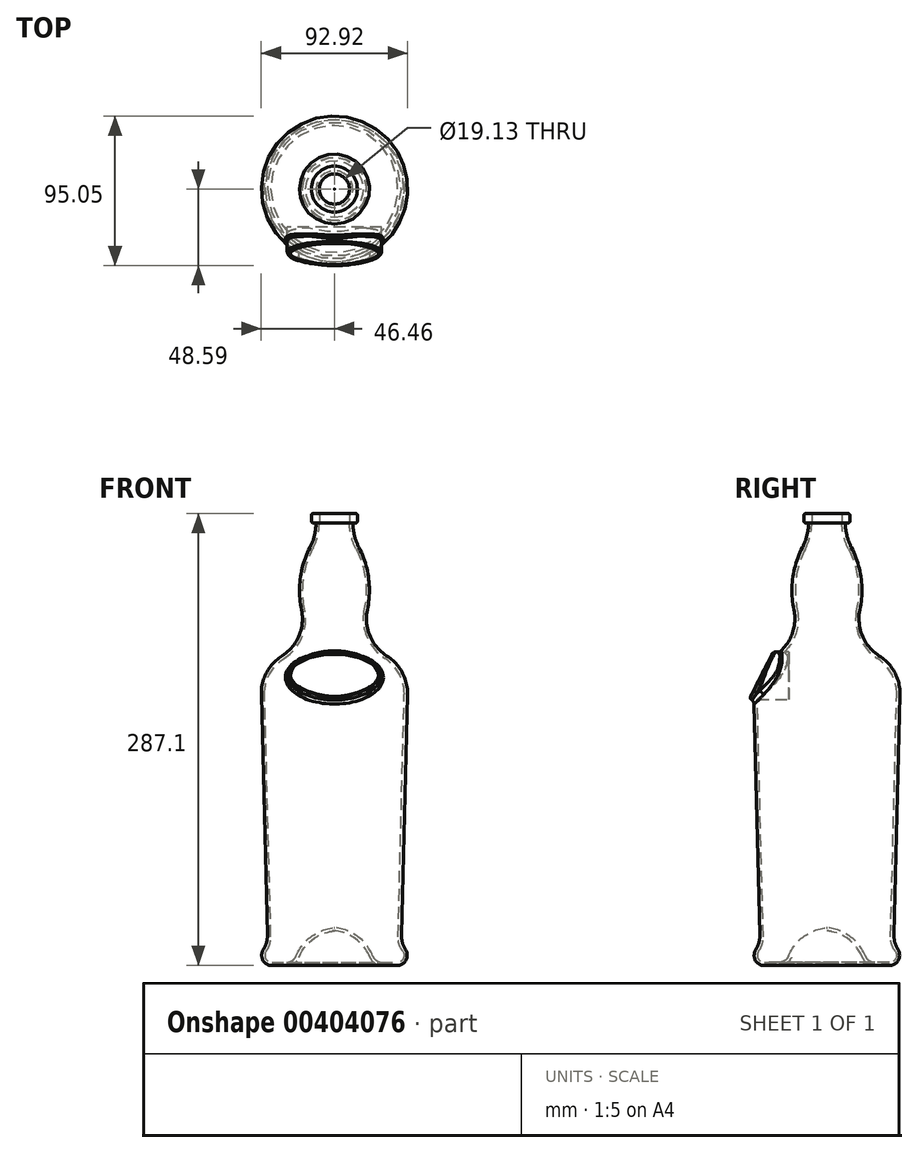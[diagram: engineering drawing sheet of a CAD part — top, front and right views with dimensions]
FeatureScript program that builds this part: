
annotation { "Feature Type Name" : "Feature", "Feature Type Description" : "" }
export const myFeature = defineFeature(function(context is Context, id is Id, definition is map)
    precondition{}
    {
        {
            var Q0;
            Q0=qCreatedBy(makeId("Front.planeOp"),FACE);
            var sketch = newSketch(context, id + "F0", { "sketchPlane" : qUnion([Q0])});
            skLineSegment(sketch, "E0", {"start": v(30.45, 0.13) * mm, "end": v(39.69, 0.13) * mm});
            skArc(sketch, "E1", {"start": v(39.69, 0.13) * mm, "mid": v(45.41, 3.52) * mm, "end": v(45.2, 10.17) * mm});
            skLineSegment(sketch, "E2.trimOffspring", {"start": v(42.6, 19.54) * mm, "end": v(46.45, 171.94) * mm});
            skArc(sketch, "E3", {"start": v(20.93, 226.15) * mm, "mid": v(22.49, 209.63) * mm, "end": v(33.17, 196.93) * mm});
            skArc(sketch, "E4", {"start": v(22.49, 5.48) * mm, "mid": v(13.58, 16.96) * mm, "end": v(0, 22.15) * mm});
            skArc(sketch, "E5", {"start": v(22.49, 5.48) * mm, "mid": v(25.65, 1.6) * mm, "end": v(30.45, 0.13) * mm});
            skArc(sketch, "E6", {"start": v(46.45, 171.94) * mm, "mid": v(43.1, 186.18) * mm, "end": v(33.17, 196.93) * mm});
            skLineSegment(sketch, "E7.bottom", {"start": v(10.27, 287.23) * mm, "end": v(13.58, 287.23) * mm});
            skLineSegment(sketch, "E7.top", {"start": v(13.08, 281.12) * mm, "end": v(13.18, 281.12) * mm});
            skLineSegment(sketch, "E7.left", {"start": v(9.57, 286.52) * mm, "end": v(9.57, 281.12) * mm});
            skLineSegment(sketch, "E7.right", {"start": v(14.58, 286.22) * mm, "end": v(14.58, 282.53) * mm});
            skArc(sketch, "E8", {"start": v(11.73, 279.7) * mm, "mid": v(12.94, 272.43) * mm, "end": v(15.62, 265.57) * mm});
            skArc(sketch, "E9", {"start": v(20.93, 226.15) * mm, "mid": v(21.7, 246.32) * mm, "end": v(15.62, 265.57) * mm});
            skPoint(sketch, "E10.visualSharp", {"position": v(11.67, 281.12) * mm});
            skArc(sketch, "E10.filletArc", {"start": v(13.08, 281.12) * mm, "mid": v(12.1, 280.7) * mm, "end": v(11.73, 279.7) * mm});
            skPoint(sketch, "E11.visualSharp", {"position": v(14.58, 281.12) * mm});
            skArc(sketch, "E11.filletArc", {"start": v(13.18, 281.12) * mm, "mid": v(14.17, 281.53) * mm, "end": v(14.58, 282.53) * mm});
            skPoint(sketch, "E12.visualSharp", {"position": v(14.58, 287.23) * mm});
            skArc(sketch, "E12.filletArc", {"start": v(14.58, 286.22) * mm, "mid": v(14.3, 286.93) * mm, "end": v(13.58, 287.23) * mm});
            skPoint(sketch, "E13.visualSharp", {"position": v(9.57, 287.23) * mm});
            skArc(sketch, "E13.filletArc", {"start": v(10.27, 287.23) * mm, "mid": v(9.77, 287.02) * mm, "end": v(9.57, 286.52) * mm});
            skArc(sketch, "E14.1", {"start": v(9.6, 280.4) * mm, "mid": v(10.8, 272.28) * mm, "end": v(13.76, 264.6) * mm});
            skArc(sketch, "E14.2", {"start": v(18.88, 226.59) * mm, "mid": v(19.6, 246.04) * mm, "end": v(13.76, 264.6) * mm});
            skArc(sketch, "E14.3", {"start": v(18.88, 226.59) * mm, "mid": v(20.55, 208.82) * mm, "end": v(32.04, 195.16) * mm});
            skArc(sketch, "E14.4", {"start": v(44.35, 171.9) * mm, "mid": v(41.26, 185.15) * mm, "end": v(32.04, 195.16) * mm});
            skLineSegment(sketch, "E15", {"start": v(9.57, 281.12) * mm, "end": v(9.6, 280.4) * mm});
            skArc(sketch, "E16.1", {"start": v(24.34, 6.24) * mm, "mid": v(14.77, 18.57) * mm, "end": v(0.18, 24.14) * mm});
            skArc(sketch, "E16.2", {"start": v(24.34, 6.24) * mm, "mid": v(26.77, 3.25) * mm, "end": v(30.45, 2.13) * mm});
            skLineSegment(sketch, "E16.3", {"start": v(30.45, 2.13) * mm, "end": v(39.69, 2.13) * mm});
            skArc(sketch, "E16.4", {"start": v(39.69, 2.13) * mm, "mid": v(43.74, 4.64) * mm, "end": v(43.3, 9.39) * mm});
            skLineSegment(sketch, "E17", {"start": v(0, 22.15) * mm, "end": v(0, 24.14) * mm});
            skLineSegment(sketch, "E18", {"start": v(0, 24.14) * mm, "end": v(0.18, 24.14) * mm});
            skArc(sketch, "E19", {"start": v(42.6, 19.54) * mm, "mid": v(43.2, 14.66) * mm, "end": v(45.2, 10.17) * mm});
            skArc(sketch, "E20", {"start": v(40.42, 18.35) * mm, "mid": v(41.1, 13.63) * mm, "end": v(43.3, 9.39) * mm});
            skLineSegment(sketch, "E21", {"start": v(40.42, 18.35) * mm, "end": v(44.35, 171.9) * mm});
            skSolve(sketch);
        }
        {
            var Q0;
            Q0=makeQuery(id+"F0.imprint","IMPRINT",FACE,{"disambiguationData":[TD([[makeQuery(id+"F0.imprint","IMPRINT",EDGE,{"derivedFrom":sQuery(id+"F0.wireOp",EDGE,"E0")}),1.0]])]});
            var Q1;
            Q1=sQuery(id+"F0.wireOp",EDGE,"E17");
            revolve(context, id + "F1", {"entities" : qUnion([Q0]), "axis" : qUnion([Q1]), "revolveType" : RevolveType.FULL});
        }
        {
            var Q0;
            Q0=qCreatedBy(makeId("Front.planeOp"),FACE);
            var sketch = newSketch(context, id + "F2", { "sketchPlane" : qUnion([Q0])});
            skEllipse(sketch, "E22", {"center": v(0, 184.17) * mm, "majorRadius": 30 * mm, "minorRadius": 15 * mm, "majorAxis": v(1, 0)});
            skSolve(sketch);
        }
        {
            var Q0;
            Q0 = qSketchRegion(id + "F2", true);
            extrude(context, id + "F3", {"entities" : qUnion([Q0]), "operationType" : NewBodyOperationType.ADD, "depth" : 65.8 * mm, "hasSecondDirection" : true, "secondDirectionOppositeDirection" : false, "secondDirectionDepth" : 24 * mm});
        }
        {
            var Q0;
            Q0=qCreatedBy(makeId("Right.planeOp"),FACE);
            var sketch = newSketch(context, id + "F4", { "sketchPlane" : qUnion([Q0])});
            skLineSegment(sketch, "E23", {"start": v(-30, 207.5) * mm, "end": v(-52.35, 163.44) * mm});
            skLineSegment(sketch, "E24", {"start": v(-52.35, 163.44) * mm, "end": v(-86.95, 163.44) * mm});
            skLineSegment(sketch, "E25", {"start": v(-86.95, 163.44) * mm, "end": v(-86.95, 207.5) * mm});
            skLineSegment(sketch, "E26", {"start": v(-86.95, 207.5) * mm, "end": v(-30, 207.5) * mm});
            skSolve(sketch);
        }
        {
            var Q0;
            Q0=makeQuery(id+"F4.imprint","IMPRINT",FACE,{"disambiguationData":[TD([[makeQuery(id+"F4.imprint","IMPRINT",EDGE,{"derivedFrom":sQuery(id+"F4.wireOp",EDGE,"E23")}),-1.0]])]});
            extrude(context, id + "F5", {"entities" : qUnion([Q0]), "endBound" : BoundingType.SYMMETRIC, "depth" : 68.8 * mm});
        }
        {
            var Q0;
            Q0=makeQuery(id+"F5.opExtrude","SWEPT_BODY",BODY,{"disambiguationData":[OSD([sQuery(id+"F4.wireOp",EDGE,"E23"),sQuery(id+"F4.wireOp",EDGE,"E24"),sQuery(id+"F4.wireOp",EDGE,"E25"),sQuery(id+"F4.wireOp",EDGE,"E26")])]});
            var Q1;
            Q1=makeQuery(id+"F1.opRevolve","SWEPT_BODY",BODY,{"disambiguationData":[OSD([sQuery(id+"F0.wireOp",EDGE,"E0"),sQuery(id+"F0.wireOp",EDGE,"E1"),sQuery(id+"F0.wireOp",EDGE,"E2.trimOffspring"),sQuery(id+"F0.wireOp",EDGE,"E3"),sQuery(id+"F0.wireOp",EDGE,"E4"),sQuery(id+"F0.wireOp",EDGE,"E5"),sQuery(id+"F0.wireOp",EDGE,"E6"),sQuery(id+"F0.wireOp",EDGE,"E7.bottom"),sQuery(id+"F0.wireOp",EDGE,"E7.top"),sQuery(id+"F0.wireOp",EDGE,"E7.left"),sQuery(id+"F0.wireOp",EDGE,"E7.right"),sQuery(id+"F0.wireOp",EDGE,"E8"),sQuery(id+"F0.wireOp",EDGE,"E9"),sQuery(id+"F0.wireOp",EDGE,"E10.filletArc"),sQuery(id+"F0.wireOp",EDGE,"E11.filletArc"),sQuery(id+"F0.wireOp",EDGE,"E12.filletArc"),sQuery(id+"F0.wireOp",EDGE,"E13.filletArc"),sQuery(id+"F0.wireOp",EDGE,"E14.1"),sQuery(id+"F0.wireOp",EDGE,"E14.2"),sQuery(id+"F0.wireOp",EDGE,"E14.3"),sQuery(id+"F0.wireOp",EDGE,"E14.4"),sQuery(id+"F0.wireOp",EDGE,"E15"),sQuery(id+"F0.wireOp",EDGE,"E16.1"),sQuery(id+"F0.wireOp",EDGE,"E16.2"),sQuery(id+"F0.wireOp",EDGE,"E16.3"),sQuery(id+"F0.wireOp",EDGE,"E16.4"),sQuery(id+"F0.wireOp",EDGE,"E17"),sQuery(id+"F0.wireOp",EDGE,"E18"),sQuery(id+"F0.wireOp",EDGE,"E19"),sQuery(id+"F0.wireOp",EDGE,"E20"),sQuery(id+"F0.wireOp",EDGE,"E21")])]});
            booleanBodies(context, id + "F6", {"operationType" : BooleanOperationType.SUBTRACTION, "tools" : qUnion([Q0]), "targets" : qUnion([Q1])});
        }
        {
            var Q0;
            Q0=makeQuery(id+"F3.boolean.opBoolean","INTERSECT",EDGE,{"derivedFrom":[makeQuery(id+"F1.opRevolve","SWEPT_FACE",FACE,{"disambiguationData":[OSD([sQuery(id+"F0.wireOp",EDGE,"E3")])]}),makeQuery(id+"F3.opExtrude","SWEPT_FACE",FACE,{"disambiguationData":[OSD([sQuery(id+"F2.wireOp",EDGE,"E22")])]})]});
            var Q1;
            Q1=makeQuery(id+"F3.boolean.opBoolean","INTERSECT",EDGE,{"disambiguationData":[OD(0.0)],"derivedFrom":[makeQuery(id+"F1.opRevolve","SWEPT_FACE",FACE,{"disambiguationData":[OSD([sQuery(id+"F0.wireOp",EDGE,"E6")])]}),makeQuery(id+"F3.opExtrude","SWEPT_FACE",FACE,{"disambiguationData":[OSD([sQuery(id+"F2.wireOp",EDGE,"E22")])]})]});
            var Q2;
            Q2=makeQuery(id+"F3.boolean.opBoolean","INTERSECT",EDGE,{"derivedFrom":[makeQuery(id+"F1.opRevolve","SWEPT_FACE",FACE,{"disambiguationData":[OSD([sQuery(id+"F0.wireOp",EDGE,"E2.trimOffspring")])]}),makeQuery(id+"F3.opExtrude","SWEPT_FACE",FACE,{"disambiguationData":[OSD([sQuery(id+"F2.wireOp",EDGE,"E22")])]})]});
            var Q3;
            Q3=makeQuery(id+"F3.boolean.opBoolean","INTERSECT",EDGE,{"disambiguationData":[OD(1.0)],"derivedFrom":[makeQuery(id+"F1.opRevolve","SWEPT_FACE",FACE,{"disambiguationData":[OSD([sQuery(id+"F0.wireOp",EDGE,"E6")])]}),makeQuery(id+"F3.opExtrude","SWEPT_FACE",FACE,{"disambiguationData":[OSD([sQuery(id+"F2.wireOp",EDGE,"E22")])]})]});
            fillet(context, id + "F7", {"entities" : qUnion([Q0, Q1, Q2, Q3]), "radius" : 3 * mm, "tangentPropagation" : true, "allowEdgeOverflow" : false});
        }
        {
            var Q0;
            {var subQ0=sQuery(id+"F2.wireOp",EDGE,"E22");Q0=makeQuery(id+"F6.opBoolean","INTERSECT",EDGE,{"derivedFrom":[makeQuery(id+"F3.boolean.opBoolean","SPLIT",FACE,{"disambiguationData":[TD([makeQuery(id+"F1.opRevolve","SWEPT_FACE",FACE,{"disambiguationData":[OSD([sQuery(id+"F0.wireOp",EDGE,"E2.trimOffspring")])]})])],"derivedFrom":makeQuery(id+"F3.opExtrude","SWEPT_FACE",FACE,{"disambiguationData":[OSD([subQ0])]})}),makeQuery(id+"F5.opExtrude","SWEPT_FACE",FACE,{"disambiguationData":[OSD([sQuery(id+"F4.wireOp",EDGE,"E23")])]})]});}
            fillet(context, id + "F8", {"entities" : qUnion([Q0]), "radius" : 2 * mm, "tangentPropagation" : true, "allowEdgeOverflow" : false});
        }
        {
            var Q0;
            Q0=makeQuery(id+"F6.opBoolean","COPY",FACE,{"derivedFrom":makeQuery(id+"F5.opExtrude","SWEPT_FACE",FACE,{"disambiguationData":[OSD([sQuery(id+"F4.wireOp",EDGE,"E23")])]})});
            extrude(context, id + "F9", {"entities" : qUnion([Q0]), "operationType" : NewBodyOperationType.REMOVE, "oppositeDirection" : true, "depth" : 1.5 * mm});
        }
        {
            var Q0;
            {var subQ0=sQuery(id+"F4.wireOp",EDGE,"E23");var subQ1=makeQuery(id+"F5.opExtrude","SWEPT_FACE",FACE,{"disambiguationData":[OSD([subQ0])]});var subQ2=sQuery(id+"F2.wireOp",EDGE,"E22");var subQ3=makeQuery(id+"F8.opFillet","BLEND_EDGE",EDGE,{"disambiguationData":[OD(1.0)],"blendedFrom":[makeQuery(id+"F6.opBoolean","INTERSECT",EDGE,{"derivedFrom":[makeQuery(id+"F3.boolean.opBoolean","SPLIT",FACE,{"disambiguationData":[TD([makeQuery(id+"F1.opRevolve","SWEPT_FACE",FACE,{"disambiguationData":[OSD([sQuery(id+"F0.wireOp",EDGE,"E2.trimOffspring")])]})])],"derivedFrom":makeQuery(id+"F3.opExtrude","SWEPT_FACE",FACE,{"disambiguationData":[OSD([subQ2])]})}),subQ1]}),makeQuery(id+"F6.opBoolean","COPY",FACE,{"derivedFrom":subQ1})],"blendedInto":[makeQuery(id+"F6.opBoolean","COPY",FACE,{"derivedFrom":subQ1})]});Q0=makeQuery(id+"F9.boolean.opBoolean","MERGE",EDGE,{"derivedFrom":[subQ3,makeQuery(id+"F9.opExtrude","CAP_EDGE",EDGE,{"disambiguationData":[OSD([subQ2,subQ0]),TDD([subQ3])],"isStart":true})]});}
            var Q1;
            {var subQ0=sQuery(id+"F4.wireOp",EDGE,"E23");var subQ1=makeQuery(id+"F5.opExtrude","SWEPT_FACE",FACE,{"disambiguationData":[OSD([subQ0])]});var subQ2=sQuery(id+"F2.wireOp",EDGE,"E22");var subQ3=makeQuery(id+"F8.opFillet","BLEND_EDGE",EDGE,{"disambiguationData":[OD(0.0)],"blendedFrom":[makeQuery(id+"F6.opBoolean","INTERSECT",EDGE,{"derivedFrom":[makeQuery(id+"F3.boolean.opBoolean","SPLIT",FACE,{"disambiguationData":[TD([makeQuery(id+"F1.opRevolve","SWEPT_FACE",FACE,{"disambiguationData":[OSD([sQuery(id+"F0.wireOp",EDGE,"E2.trimOffspring")])]})])],"derivedFrom":makeQuery(id+"F3.opExtrude","SWEPT_FACE",FACE,{"disambiguationData":[OSD([subQ2])]})}),subQ1]}),makeQuery(id+"F6.opBoolean","COPY",FACE,{"derivedFrom":subQ1})],"blendedInto":[makeQuery(id+"F6.opBoolean","COPY",FACE,{"derivedFrom":subQ1})]});Q1=makeQuery(id+"F9.boolean.opBoolean","MERGE",EDGE,{"derivedFrom":[subQ3,makeQuery(id+"F9.opExtrude","CAP_EDGE",EDGE,{"disambiguationData":[OSD([subQ2,subQ0]),TDD([subQ3])],"isStart":true})]});}
            var Q2;
            {var subQ0=sQuery(id+"F4.wireOp",EDGE,"E23");var subQ1=makeQuery(id+"F5.opExtrude","SWEPT_FACE",FACE,{"disambiguationData":[OSD([subQ0])]});var subQ2=sQuery(id+"F2.wireOp",EDGE,"E22");Q2=makeQuery(id+"F9.boolean.opBoolean","COPY",EDGE,{"derivedFrom":makeQuery(id+"F9.opExtrude","CAP_EDGE",EDGE,{"disambiguationData":[OSD([subQ2,subQ0]),TDD([makeQuery(id+"F8.opFillet","BLEND_EDGE",EDGE,{"disambiguationData":[OD(1.0)],"blendedFrom":[makeQuery(id+"F6.opBoolean","INTERSECT",EDGE,{"derivedFrom":[makeQuery(id+"F3.boolean.opBoolean","SPLIT",FACE,{"disambiguationData":[TD([makeQuery(id+"F1.opRevolve","SWEPT_FACE",FACE,{"disambiguationData":[OSD([sQuery(id+"F0.wireOp",EDGE,"E2.trimOffspring")])]})])],"derivedFrom":makeQuery(id+"F3.opExtrude","SWEPT_FACE",FACE,{"disambiguationData":[OSD([subQ2])]})}),subQ1]}),makeQuery(id+"F6.opBoolean","COPY",FACE,{"derivedFrom":subQ1})],"blendedInto":[makeQuery(id+"F6.opBoolean","COPY",FACE,{"derivedFrom":subQ1})]})])],"isStart":false})});}
            var Q3;
            {var subQ0=sQuery(id+"F4.wireOp",EDGE,"E23");var subQ1=makeQuery(id+"F5.opExtrude","SWEPT_FACE",FACE,{"disambiguationData":[OSD([subQ0])]});var subQ2=sQuery(id+"F2.wireOp",EDGE,"E22");Q3=makeQuery(id+"F9.boolean.opBoolean","COPY",EDGE,{"derivedFrom":makeQuery(id+"F9.opExtrude","CAP_EDGE",EDGE,{"disambiguationData":[OSD([subQ2,subQ0]),TDD([makeQuery(id+"F8.opFillet","BLEND_EDGE",EDGE,{"disambiguationData":[OD(0.0)],"blendedFrom":[makeQuery(id+"F6.opBoolean","INTERSECT",EDGE,{"derivedFrom":[makeQuery(id+"F3.boolean.opBoolean","SPLIT",FACE,{"disambiguationData":[TD([makeQuery(id+"F1.opRevolve","SWEPT_FACE",FACE,{"disambiguationData":[OSD([sQuery(id+"F0.wireOp",EDGE,"E2.trimOffspring")])]})])],"derivedFrom":makeQuery(id+"F3.opExtrude","SWEPT_FACE",FACE,{"disambiguationData":[OSD([subQ2])]})}),subQ1]}),makeQuery(id+"F6.opBoolean","COPY",FACE,{"derivedFrom":subQ1})],"blendedInto":[makeQuery(id+"F6.opBoolean","COPY",FACE,{"derivedFrom":subQ1})]})])],"isStart":false})});}
            fillet(context, id + "F10", {"entities" : qUnion([Q0, Q1, Q2, Q3]), "radius" : 0.5 * mm, "allowEdgeOverflow" : false});
        }
    });
